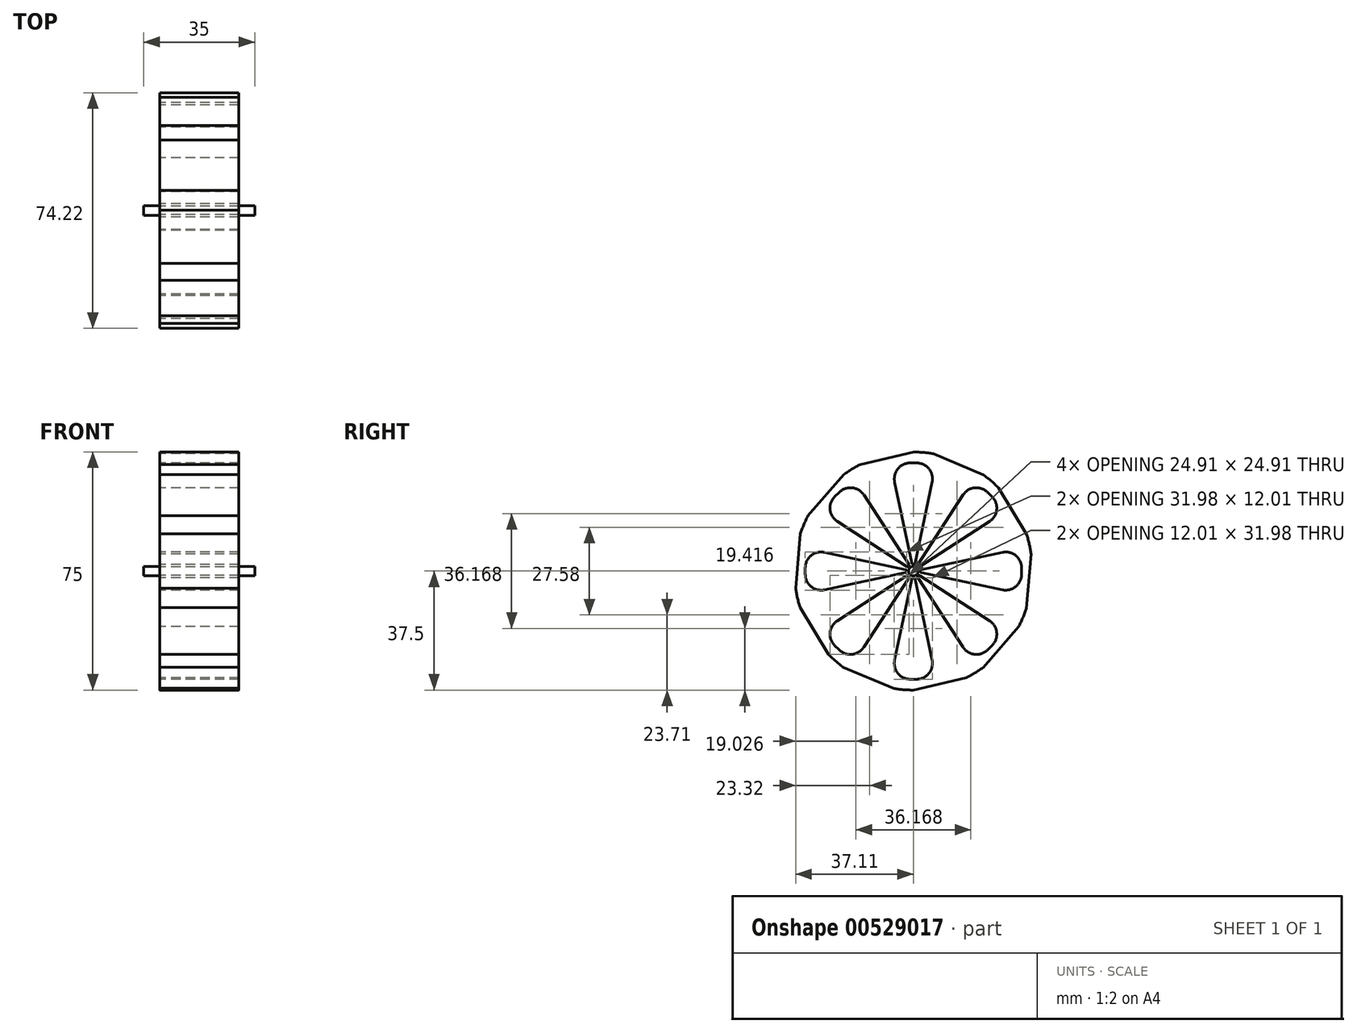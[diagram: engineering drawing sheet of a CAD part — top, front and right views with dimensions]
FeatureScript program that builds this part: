
annotation { "Feature Type Name" : "Feature", "Feature Type Description" : "" }
export const myFeature = defineFeature(function(context is Context, id is Id, definition is map)
    precondition{}
    {
        {
            var Q0;
            Q0=qCreatedBy(makeId("Right.planeOp"),FACE);
            var sketch = newSketch(context, id + "F0", { "sketchPlane" : qUnion([Q0])});
            skCircle(sketch, "E0", {"center": v(0, 0) * mm, "radius": 37.5 * mm});
            skSolve(sketch);
        }
        {
            var Q0;
            Q0 = qSketchRegion(id + "F0", true);
            extrude(context, id + "F1", {"entities" : qUnion([Q0]), "endBound" : BoundingType.SYMMETRIC, "depth" : 25 * mm, "offsetDistance" : 25 * mm});
        }
        {
            var Q0;
            Q0=qCreatedBy(makeId("Right.planeOp"),FACE);
            var sketch = newSketch(context, id + "F2", { "sketchPlane" : qUnion([Q0])});
            skLineSegment(sketch, "E1.top", {"start": v(1, 34.08) * mm, "end": v(-1, 34.08) * mm});
            skPoint(sketch, "E1.middle", {"position": v(0, 17.13) * mm});
            skLineSegment(sketch, "E2", {"start": v(-5.9, 28.04) * mm, "end": v(-0.49, 2.49) * mm});
            skLineSegment(sketch, "E3", {"start": v(0.49, 2.49) * mm, "end": v(5.9, 28.04) * mm});
            skPoint(sketch, "E4.orphan", {"position": v(-7.18, 0.18) * mm});
            skPoint(sketch, "E1.bottom.start.orphan", {"position": v(7.18, 0.18) * mm});
            skPoint(sketch, "E5.visualSharp", {"position": v(-7.18, 34.08) * mm});
            skArc(sketch, "E5.filletArc", {"start": v(-1, 34.08) * mm, "mid": v(-4.9, 32.22) * mm, "end": v(-5.9, 28.04) * mm});
            skPoint(sketch, "E6.visualSharp", {"position": v(7.18, 34.08) * mm});
            skArc(sketch, "E6.filletArc", {"start": v(5.9, 28.04) * mm, "mid": v(4.9, 32.22) * mm, "end": v(1, 34.08) * mm});
            skPoint(sketch, "E7.visualSharp", {"position": v(0, 0.18) * mm});
            skArc(sketch, "E7.filletArc", {"start": v(-0.49, 2.49) * mm, "mid": v(0, 2.1) * mm, "end": v(0.49, 2.49) * mm});
            skSolve(sketch);
        }
        {
            var Q0;
            Q0 = qSketchRegion(id + "F2", true);
            extrude(context, id + "F3", {"entities" : qUnion([Q0]), "operationType" : NewBodyOperationType.REMOVE, "endBound" : BoundingType.SYMMETRIC, "depth" : 25 * mm, "offsetDistance" : 25 * mm});
        }
        {
            var Q0;
            Q0=makeQuery(id+"F3.boolean.opBoolean","COPY",FACE,{"derivedFrom":makeQuery(id+"F3.opExtrude","SWEPT_FACE",FACE,{"disambiguationData":[OSD([sQuery(id+"F2.wireOp",EDGE,"E2")])]})});
            var Q1;
            Q1=makeQuery(id+"F3.boolean.opBoolean","COPY",FACE,{"derivedFrom":makeQuery(id+"F3.opExtrude","SWEPT_FACE",FACE,{"disambiguationData":[OSD([sQuery(id+"F2.wireOp",EDGE,"E5.filletArc")])]})});
            var Q2;
            Q2=makeQuery(id+"F3.boolean.opBoolean","COPY",FACE,{"derivedFrom":makeQuery(id+"F3.opExtrude","SWEPT_FACE",FACE,{"disambiguationData":[OSD([sQuery(id+"F2.wireOp",EDGE,"E1.top")])]})});
            var Q3;
            Q3=makeQuery(id+"F3.boolean.opBoolean","COPY",FACE,{"derivedFrom":makeQuery(id+"F3.opExtrude","SWEPT_FACE",FACE,{"disambiguationData":[OSD([sQuery(id+"F2.wireOp",EDGE,"E6.filletArc")])]})});
            var Q4;
            Q4=makeQuery(id+"F3.boolean.opBoolean","COPY",FACE,{"derivedFrom":makeQuery(id+"F3.opExtrude","SWEPT_FACE",FACE,{"disambiguationData":[OSD([sQuery(id+"F2.wireOp",EDGE,"E3")])]})});
            var Q5;
            Q5=makeQuery(id+"F3.boolean.opBoolean","COPY",FACE,{"derivedFrom":makeQuery(id+"F3.opExtrude","SWEPT_FACE",FACE,{"disambiguationData":[OSD([sQuery(id+"F2.wireOp",EDGE,"E7.filletArc")])]})});
            var Q6;
            Q6=makeQuery(id+"F1.opExtrude","CAP_EDGE",EDGE,{"disambiguationData":[OSD([sQuery(id+"F0.wireOp",EDGE,"E0")])],"isStart":false});
            circularPattern(context, id + "F4", {"patternType" : PatternType.FACE, "faces" : qUnion([Q0, Q1, Q2, Q3, Q4, Q5]), "axis" : qUnion([Q6]), "angle" : 360 * degree, "instanceCount" : 8, "equalSpace" : true});
        }
        {
            var Q0;
            Q0=qCreatedBy(makeId("Right.planeOp"),FACE);
            var sketch = newSketch(context, id + "F5", { "sketchPlane" : qUnion([Q0])});
            skCircle(sketch, "E8.cCircle", {"center": v(0, 0) * mm, "radius": 36.5 * mm, "construction": true});
            skLineSegment(sketch, "E8.0", {"start": v(25.15, 29) * mm, "end": v(37.39, 8.67) * mm});
            skLineSegment(sketch, "E8.1", {"start": v(37.39, 8.67) * mm, "end": v(35.34, -14.96) * mm});
            skLineSegment(sketch, "E8.2", {"start": v(35.34, -14.96) * mm, "end": v(19.8, -32.88) * mm});
            skLineSegment(sketch, "E8.3", {"start": v(19.8, -32.88) * mm, "end": v(-3.3, -38.24) * mm});
            skLineSegment(sketch, "E8.4", {"start": v(-3.3, -38.24) * mm, "end": v(-25.15, -29) * mm});
            skLineSegment(sketch, "E8.5", {"start": v(-25.15, -29) * mm, "end": v(-37.39, -8.67) * mm});
            skLineSegment(sketch, "E8.6", {"start": v(-37.39, -8.67) * mm, "end": v(-35.34, 14.96) * mm});
            skLineSegment(sketch, "E8.7", {"start": v(-35.34, 14.96) * mm, "end": v(-19.8, 32.88) * mm});
            skLineSegment(sketch, "E8.8", {"start": v(-19.8, 32.88) * mm, "end": v(3.3, 38.24) * mm});
            skLineSegment(sketch, "E8.9", {"start": v(3.3, 38.24) * mm, "end": v(25.15, 29) * mm});
            skPoint(sketch, "E8.0.midPoint", {"position": v(31.27, 18.83) * mm});
            skSolve(sketch);
        }
        {
            var Q0;
            Q0 = qSketchRegion(id + "F5", true);
            extrude(context, id + "F6", {"entities" : qUnion([Q0]), "operationType" : NewBodyOperationType.INTERSECT, "endBound" : BoundingType.SYMMETRIC, "oppositeDirection" : true, "depth" : 25 * mm, "offsetDistance" : 25 * mm});
        }
        {
            var Q0;
            Q0=qCreatedBy(makeId("Right.planeOp"),FACE);
            var sketch = newSketch(context, id + "F7", { "sketchPlane" : qUnion([Q0])});
            skCircle(sketch, "E9", {"center": v(0, 0) * mm, "radius": 1.5 * mm});
            skSolve(sketch);
        }
        {
            var Q0;
            Q0 = qSketchRegion(id + "F7", true);
            extrude(context, id + "F8", {"entities" : qUnion([Q0]), "operationType" : NewBodyOperationType.ADD, "endBound" : BoundingType.SYMMETRIC, "depth" : 35 * mm, "offsetDistance" : 25 * mm});
        }
    });
